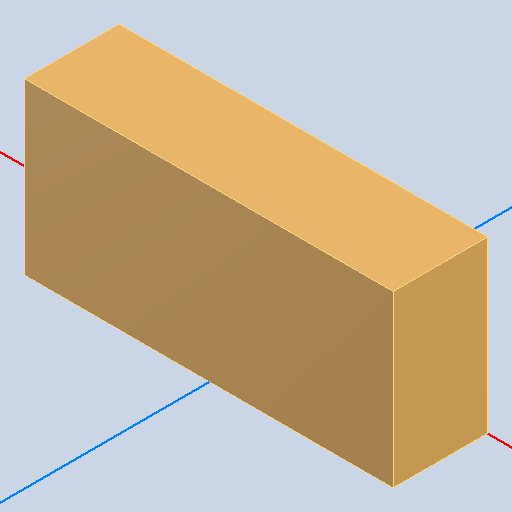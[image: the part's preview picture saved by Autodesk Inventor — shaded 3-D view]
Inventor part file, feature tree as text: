
AUTODESK INVENTOR PART (.ipt)
format: ipt  version: 2022 (Build 260153000, 153)  size: 92,160 bytes
history: native  units: mm
features: other x2, extrude x1
ambient origin geometry x8: Origin, YZ Plane, XZ Plane, XY Plane, X Axis, Y Axis, Z Axis, Center Point
bodies: Body1 (feature_tree)
feature tree (3):
  other  "Твердое тело1"
  extrude  "Выдавливание1"  Depth=1.0mm TaperAngle=0.0deg
  other  "SOD-123_MINI-SMA, CGRM4004-G_13"
